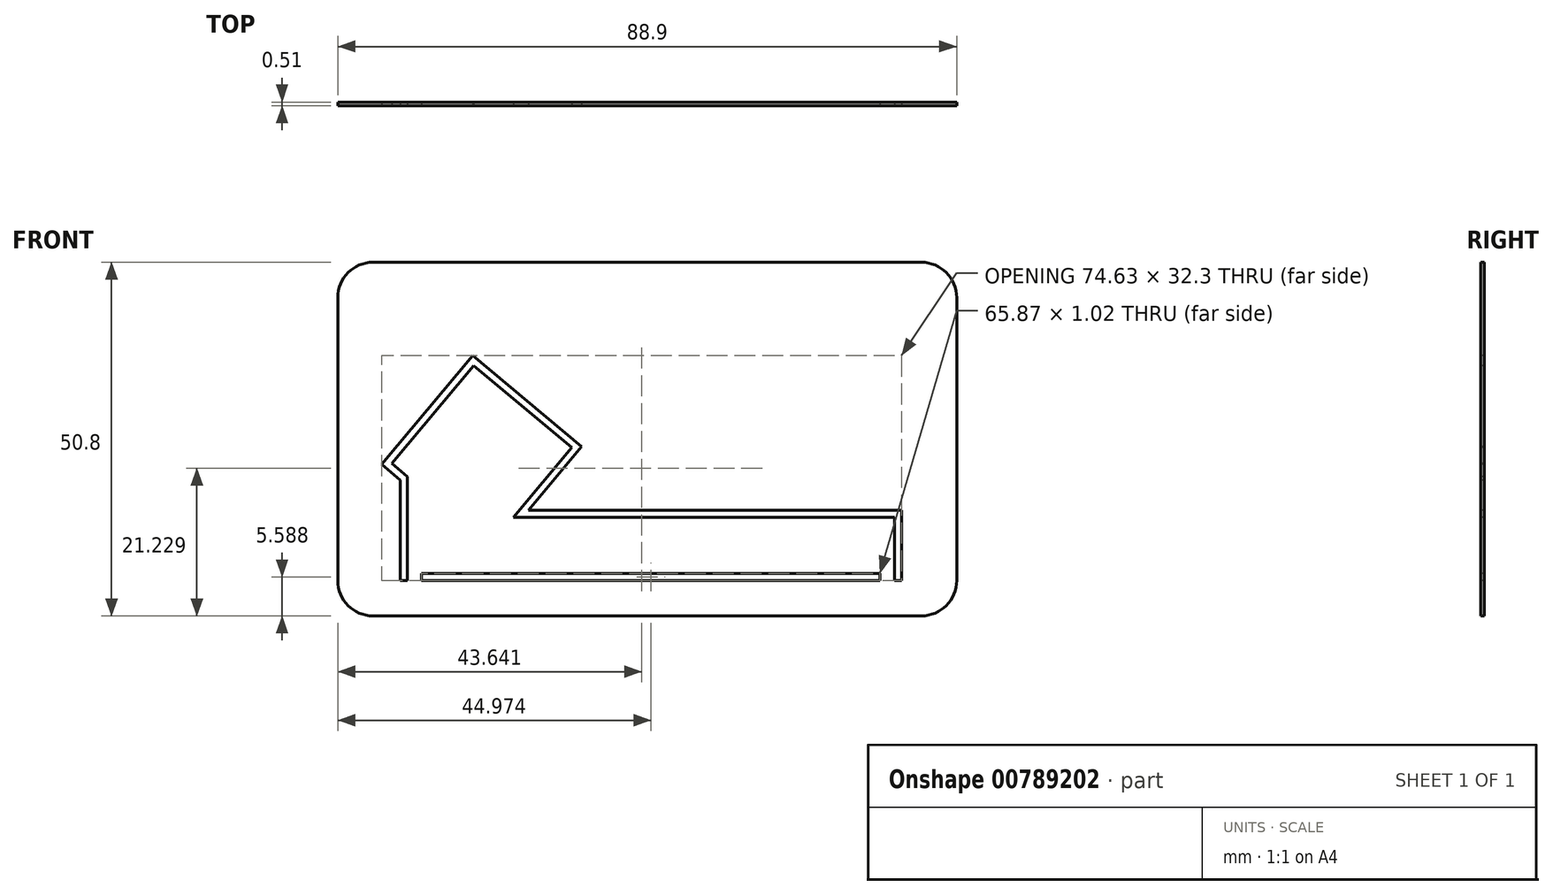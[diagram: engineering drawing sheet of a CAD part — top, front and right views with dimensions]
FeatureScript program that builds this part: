
annotation { "Feature Type Name" : "Feature", "Feature Type Description" : "" }
export const myFeature = defineFeature(function(context is Context, id is Id, definition is map)
    precondition{}
    {
        {
            var Q0;
            Q0=qCreatedBy(makeId("Front.planeOp"),FACE);
            var sketch = newSketch(context, id + "F0", { "sketchPlane" : qUnion([Q0])});
            skLineSegment(sketch, "E0.bottom", {"start": v(-39.37, 25.4) * mm, "end": v(39.37, 25.4) * mm});
            skLineSegment(sketch, "E0.top", {"start": v(-39.37, -25.4) * mm, "end": v(39.37, -25.4) * mm});
            skLineSegment(sketch, "E0.left", {"start": v(-44.45, 20.32) * mm, "end": v(-44.45, -20.32) * mm});
            skLineSegment(sketch, "E0.right", {"start": v(44.45, 20.32) * mm, "end": v(44.45, -20.32) * mm});
            skPoint(sketch, "E1.visualSharp", {"position": v(-44.45, 25.4) * mm});
            skArc(sketch, "E1.filletArc", {"start": v(-39.37, 25.4) * mm, "mid": v(-42.96, 23.91) * mm, "end": v(-44.45, 20.32) * mm});
            skPoint(sketch, "E2.visualSharp", {"position": v(44.45, 25.4) * mm});
            skArc(sketch, "E2.filletArc", {"start": v(44.45, 20.32) * mm, "mid": v(42.96, 23.91) * mm, "end": v(39.37, 25.4) * mm});
            skPoint(sketch, "E3.visualSharp", {"position": v(44.45, -25.4) * mm});
            skArc(sketch, "E3.filletArc", {"start": v(39.37, -25.4) * mm, "mid": v(42.96, -23.91) * mm, "end": v(44.45, -20.32) * mm});
            skPoint(sketch, "E4.visualSharp", {"position": v(-44.45, -25.4) * mm});
            skArc(sketch, "E4.filletArc", {"start": v(-44.45, -20.32) * mm, "mid": v(-42.96, -23.91) * mm, "end": v(-39.37, -25.4) * mm});
            skSolve(sketch);
        }
        {
            var Q0;
            Q0 = qSketchRegion(id + "F0", true);
            extrude(context, id + "F1", {"entities" : qUnion([Q0]), "depth" : 0.5 * mm, "offsetDistance" : 25.4 * mm});
        }
        {
            var Q0;
            Q0=makeQuery(id+"F1.opExtrude","CAP_FACE",FACE,{"disambiguationData":[OSD([sQuery(id+"F0.wireOp",EDGE,"E0.bottom"),sQuery(id+"F0.wireOp",EDGE,"E0.top"),sQuery(id+"F0.wireOp",EDGE,"E0.left"),sQuery(id+"F0.wireOp",EDGE,"E0.right"),sQuery(id+"F0.wireOp",EDGE,"E1.filletArc"),sQuery(id+"F0.wireOp",EDGE,"E2.filletArc"),sQuery(id+"F0.wireOp",EDGE,"E3.filletArc"),sQuery(id+"F0.wireOp",EDGE,"E4.filletArc")])],"isStart":false});
            var sketch = newSketch(context, id + "F2", { "sketchPlane" : qUnion([Q0])});
            skCircle(sketch, "E5.cCircle", {"center": v(-23.77, -2.38) * mm, "radius": 9.18 * mm, "construction": true});
            skLineSegment(sketch, "E5.0", {"start": v(-10.84, -1.23) * mm, "end": v(-19.24, -11.27) * mm});
            skLineSegment(sketch, "E5.2", {"start": v(-36.7, -3.52) * mm, "end": v(-24.91, 10.55) * mm});
            skLineSegment(sketch, "E5.3", {"start": v(-24.91, 10.55) * mm, "end": v(-10.84, -1.23) * mm});
            skPoint(sketch, "E5.0.midPoint", {"position": v(-16.73, -8.27) * mm});
            skLineSegment(sketch, "E6.0", {"start": v(-38.12, -3.65) * mm, "end": v(-25.04, 11.98) * mm});
            skLineSegment(sketch, "E6.2", {"start": v(-9.41, -1.1) * mm, "end": v(-17.07, -10.25) * mm});
            skLineSegment(sketch, "E6.3", {"start": v(-25.04, 11.98) * mm, "end": v(-9.41, -1.1) * mm});
            skLineSegment(sketch, "E7", {"start": v(-35.46, -5.88) * mm, "end": v(-35.46, -20.32) * mm});
            skLineSegment(sketch, "E8.bottom", {"start": v(-32.41, -19.3) * mm, "end": v(33.46, -19.3) * mm});
            skLineSegment(sketch, "E8.top", {"start": v(-32.41, -20.32) * mm, "end": v(33.46, -20.32) * mm});
            skLineSegment(sketch, "E8.left", {"start": v(-32.41, -19.3) * mm, "end": v(-32.41, -20.32) * mm});
            skLineSegment(sketch, "E8.right", {"start": v(33.46, -19.3) * mm, "end": v(33.46, -20.32) * mm});
            skLineSegment(sketch, "E9", {"start": v(-35.46, -20.32) * mm, "end": v(-34.44, -20.32) * mm});
            skLineSegment(sketch, "E10", {"start": v(35.5, -20.32) * mm, "end": v(35.5, -11.27) * mm});
            skLineSegment(sketch, "E11", {"start": v(35.5, -11.27) * mm, "end": v(-19.24, -11.27) * mm});
            skLineSegment(sketch, "E12.0", {"start": v(36.5, -10.25) * mm, "end": v(-17.07, -10.25) * mm});
            skLineSegment(sketch, "E12.1", {"start": v(36.5, -20.32) * mm, "end": v(36.5, -10.25) * mm});
            skLineSegment(sketch, "E13", {"start": v(35.5, -20.32) * mm, "end": v(36.5, -20.32) * mm});
            skLineSegment(sketch, "E14.trimOffspring", {"start": v(-35.46, -5.88) * mm, "end": v(-38.12, -3.65) * mm});
            skLineSegment(sketch, "E15.trimOffspring", {"start": v(-34.44, -5.4) * mm, "end": v(-34.44, -20.32) * mm});
            skLineSegment(sketch, "E16.trimOffspring", {"start": v(-34.44, -5.4) * mm, "end": v(-36.7, -3.52) * mm});
            skPoint(sketch, "E17.orphan", {"position": v(-22.62, -15.3) * mm});
            skSolve(sketch);
        }
        {
            var Q0;
            Q0=makeQuery(id+"F2.imprint","IMPRINT",FACE,{"disambiguationData":[TD([[makeQuery(id+"F2.imprint","IMPRINT",EDGE,{"derivedFrom":sQuery(id+"F2.wireOp",EDGE,"E5.0")}),1.0]])]});
            var Q1;
            Q1=makeQuery(id+"F2.imprint","IMPRINT",FACE,{"disambiguationData":[TD([[makeQuery(id+"F2.imprint","IMPRINT",EDGE,{"derivedFrom":sQuery(id+"F2.wireOp",EDGE,"E8.bottom")}),-1.0]])]});
            extrude(context, id + "F3", {"entities" : qUnion([Q0, Q1]), "operationType" : NewBodyOperationType.REMOVE, "endBound" : BoundingType.THROUGH_ALL, "oppositeDirection" : true, "depth" : 25.4 * mm, "offsetDistance" : 25.4 * mm});
        }
    });
